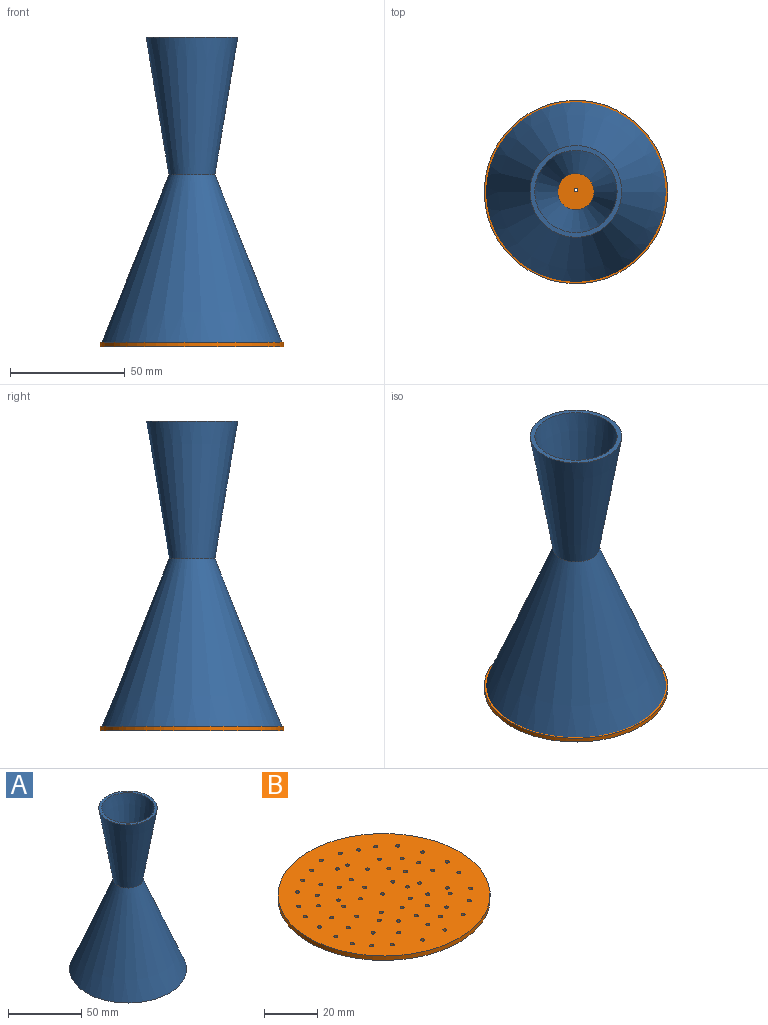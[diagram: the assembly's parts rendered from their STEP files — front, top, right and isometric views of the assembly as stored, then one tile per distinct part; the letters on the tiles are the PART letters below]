
ASSEMBLY  parts=2 mates=1
PART A: 6 faces, bbox 80x80x135 mm
  f0: plane 40x40mm, normal (0,0,1), area 241.9mm2, adj f1,f4
  f1: cone r=20mm half-angle=9.5deg, axis (0,0,1), area 5732.9mm2, adj f0,f2
  f2: cone r=10mm half-angle=21.8deg, axis (0,0,-1), area 12688.5mm2, adj f1,f3
  f3: plane 80x80mm, normal (0,0,-1), area 526.8mm2, adj f2,f5
  f4: cone r=18.03mm half-angle=9.5deg, axis (0,0,1), area 4969.3mm2, adj f0,f5
  f5: cone r=8.14mm half-angle=21.8deg, axis (0,0,-1), area 11583.3mm2, adj f3,f4
PART B: 66 faces, bbox 80x80x2 mm
  f0: cylinder r=0.75mm len=2mm, axis (0,0,-1), area 9.4mm2, adj f64,f65
  f1: cylinder r=0.75mm len=2mm, axis (0,0,-1), area 9.4mm2, adj f64,f65
  f2: cylinder r=0.75mm len=2mm, axis (0,0,-1), area 9.4mm2, adj f64,f65
  f3: cylinder r=0.75mm len=2mm, axis (0,0,-1), area 9.4mm2, adj f64,f65
  f4: cylinder r=0.75mm len=2mm, axis (0,0,-1), area 9.4mm2, adj f64,f65
  f5: cylinder r=0.75mm len=2mm, axis (0,0,-1), area 9.4mm2, adj f64,f65
  f6: cylinder r=0.75mm len=2mm, axis (0,0,-1), area 9.4mm2, adj f64,f65
  f7: cylinder r=0.75mm len=2mm, axis (0,0,-1), area 9.4mm2, adj f64,f65
  f8: cylinder r=0.75mm len=2mm, axis (0,0,-1), area 9.4mm2, adj f64,f65
  f9: cylinder r=0.75mm len=2mm, axis (0,0,-1), area 9.4mm2, adj f64,f65
  f10: cylinder r=0.75mm len=2mm, axis (0,0,-1), area 9.4mm2, adj f64,f65
  f11: cylinder r=0.75mm len=2mm, axis (0,0,-1), area 9.4mm2, adj f64,f65
  f12: cylinder r=0.75mm len=2mm, axis (0,0,-1), area 9.4mm2, adj f64,f65
  f13: cylinder r=0.75mm len=2mm, axis (0,0,-1), area 9.4mm2, adj f64,f65
  f14: cylinder r=0.75mm len=2mm, axis (0,0,-1), area 9.4mm2, adj f64,f65
  f15: cylinder r=0.75mm len=2mm, axis (0,0,-1), area 9.4mm2, adj f64,f65
  f16: cylinder r=0.75mm len=2mm, axis (0,0,-1), area 9.4mm2, adj f64,f65
  f17: cylinder r=0.75mm len=2mm, axis (0,0,-1), area 9.4mm2, adj f64,f65
  f18: cylinder r=0.75mm len=2mm, axis (0,0,-1), area 9.4mm2, adj f64,f65
  f19: cylinder r=0.75mm len=2mm, axis (0,0,-1), area 9.4mm2, adj f64,f65
  f20: cylinder r=0.75mm len=2mm, axis (0,0,-1), area 9.4mm2, adj f64,f65
  f21: cylinder r=0.75mm len=2mm, axis (0,0,-1), area 9.4mm2, adj f64,f65
  f22: cylinder r=0.75mm len=2mm, axis (0,0,-1), area 9.4mm2, adj f64,f65
  f23: cylinder r=0.75mm len=2mm, axis (0,0,-1), area 9.4mm2, adj f64,f65
  f24: cylinder r=0.75mm len=2mm, axis (0,0,-1), area 9.4mm2, adj f64,f65
  f25: cylinder r=0.75mm len=2mm, axis (0,0,-1), area 9.4mm2, adj f64,f65
  f26: cylinder r=0.75mm len=2mm, axis (0,0,-1), area 9.4mm2, adj f64,f65
  f27: cylinder r=0.75mm len=2mm, axis (0,0,-1), area 9.4mm2, adj f64,f65
  f28: cylinder r=0.75mm len=2mm, axis (0,0,-1), area 9.4mm2, adj f64,f65
  f29: cylinder r=0.75mm len=2mm, axis (0,0,-1), area 9.4mm2, adj f64,f65
  f30: cylinder r=0.75mm len=2mm, axis (0,0,-1), area 9.4mm2, adj f64,f65
  f31: cylinder r=0.75mm len=2mm, axis (0,0,-1), area 9.4mm2, adj f64,f65
  f32: cylinder r=0.75mm len=2mm, axis (0,0,-1), area 9.4mm2, adj f64,f65
  f33: cylinder r=0.75mm len=2mm, axis (0,0,-1), area 9.4mm2, adj f64,f65
  f34: cylinder r=0.75mm len=2mm, axis (0,0,-1), area 9.4mm2, adj f64,f65
  f35: cylinder r=0.75mm len=2mm, axis (0,0,-1), area 9.4mm2, adj f64,f65
  f36: cylinder r=0.75mm len=2mm, axis (0,0,-1), area 9.4mm2, adj f64,f65
  f37: cylinder r=0.75mm len=2mm, axis (0,0,-1), area 9.4mm2, adj f64,f65
  f38: cylinder r=0.75mm len=2mm, axis (0,0,-1), area 9.4mm2, adj f64,f65
  f39: cylinder r=0.75mm len=2mm, axis (0,0,-1), area 9.4mm2, adj f64,f65
  f40: cylinder r=0.75mm len=2mm, axis (0,0,-1), area 9.4mm2, adj f64,f65
  f41: cylinder r=0.75mm len=2mm, axis (0,0,-1), area 9.4mm2, adj f64,f65
  f42: cylinder r=0.75mm len=2mm, axis (0,0,-1), area 9.4mm2, adj f64,f65
  f43: cylinder r=0.75mm len=2mm, axis (0,0,-1), area 9.4mm2, adj f64,f65
  f44: cylinder r=0.75mm len=2mm, axis (0,0,-1), area 9.4mm2, adj f64,f65
  f45: cylinder r=0.75mm len=2mm, axis (0,0,-1), area 9.4mm2, adj f64,f65
  f46: cylinder r=0.75mm len=2mm, axis (0,0,-1), area 9.4mm2, adj f64,f65
  f47: cylinder r=0.75mm len=2mm, axis (0,0,-1), area 9.4mm2, adj f64,f65
  f48: cylinder r=0.75mm len=2mm, axis (0,0,-1), area 9.4mm2, adj f64,f65
  f49: cylinder r=0.75mm len=2mm, axis (0,0,-1), area 9.4mm2, adj f64,f65
  f50: cylinder r=0.75mm len=2mm, axis (0,0,-1), area 9.4mm2, adj f64,f65
  f51: cylinder r=0.75mm len=2mm, axis (0,0,-1), area 9.4mm2, adj f64,f65
  f52: cylinder r=0.75mm len=2mm, axis (0,0,-1), area 9.4mm2, adj f64,f65
  f53: cylinder r=0.75mm len=2mm, axis (0,0,-1), area 9.4mm2, adj f64,f65
  f54: cylinder r=0.75mm len=2mm, axis (0,0,-1), area 9.4mm2, adj f64,f65
  f55: cylinder r=0.75mm len=2mm, axis (0,0,-1), area 9.4mm2, adj f64,f65
  f56: cylinder r=0.75mm len=2mm, axis (0,0,-1), area 9.4mm2, adj f64,f65
  f57: cylinder r=0.75mm len=2mm, axis (0,0,-1), area 9.4mm2, adj f64,f65
  f58: cylinder r=0.75mm len=2mm, axis (0,0,-1), area 9.4mm2, adj f64,f65
  f59: cylinder r=0.75mm len=2mm, axis (0,0,-1), area 9.4mm2, adj f64,f65
  f60: cylinder r=0.75mm len=2mm, axis (0,0,-1), area 9.4mm2, adj f64,f65
  f61: cylinder r=0.75mm len=2mm, axis (0,0,-1), area 9.4mm2, adj f64,f65
  f62: cylinder r=0.75mm len=2mm, axis (0,0,-1), area 9.4mm2, adj f64,f65
  f63: cylinder r=40mm len=80mm, axis (0,0,-1), area 502.7mm2, adj f64,f65
  f64: plane 80x80mm, normal (0,0,1), area 4915.2mm2, adj f0,f1,f2,f3,f4,f5,f6,f7
  f65: plane 80x80mm, normal (0,0,-1), area 4915.2mm2, adj f0,f1,f2,f3,f4,f5,f6,f7
PLACE A at identity
PLACE B t=(0,0,-75)mm
MATE fastened B.f63 <-> A.f5  axis (0,0,-1) through (0,0,-75)mm
